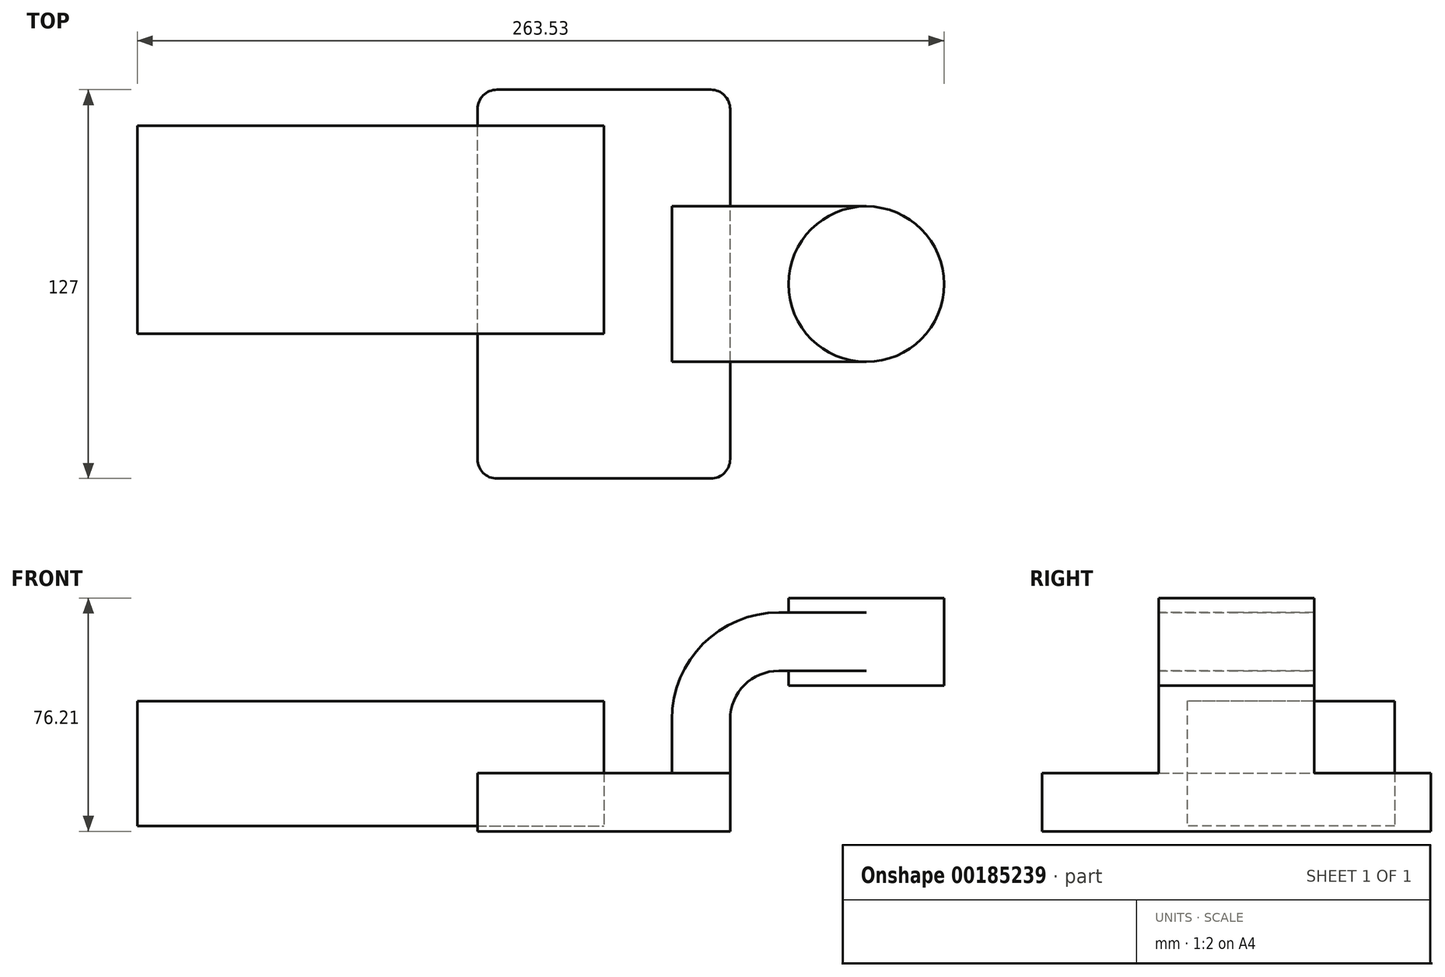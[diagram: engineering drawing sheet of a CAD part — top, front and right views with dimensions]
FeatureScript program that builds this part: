
annotation { "Feature Type Name" : "Feature", "Feature Type Description" : "" }
export const myFeature = defineFeature(function(context is Context, id is Id, definition is map)
    precondition{}
    {
        {
            var Q0;
            Q0=qCreatedBy(makeId("Front.planeOp"),FACE);
            var sketch = newSketch(context, id + "F0", { "sketchPlane" : qUnion([Q0])});
            skLineSegment(sketch, "E0.bottom", {"start": v(41.28, 9.53) * mm, "end": v(-41.28, 9.53) * mm});
            skLineSegment(sketch, "E0.top", {"start": v(41.28, -9.52) * mm, "end": v(-41.28, -9.52) * mm});
            skLineSegment(sketch, "E0.left", {"start": v(41.28, 9.53) * mm, "end": v(41.28, -9.52) * mm});
            skLineSegment(sketch, "E0.right", {"start": v(-41.28, 9.53) * mm, "end": v(-41.28, -9.52) * mm});
            skPoint(sketch, "E0.middle", {"position": v(0, 0) * mm});
            skLineSegment(sketch, "E1.bottom", {"start": v(111.12, 66.68) * mm, "end": v(60.32, 66.68) * mm});
            skLineSegment(sketch, "E1.top", {"start": v(111.12, 38.1) * mm, "end": v(60.33, 38.1) * mm});
            skLineSegment(sketch, "E1.left", {"start": v(111.12, 66.68) * mm, "end": v(111.12, 38.1) * mm});
            skLineSegment(sketch, "E1.right", {"start": v(60.32, 66.68) * mm, "end": v(60.33, 38.1) * mm});
            skPoint(sketch, "E1.middle", {"position": v(85.73, 52.39) * mm});
            skLineSegment(sketch, "E2", {"start": v(41.28, 9.53) * mm, "end": v(41.28, 27) * mm});
            skArc(sketch, "E3", {"start": v(41.28, 27) * mm, "mid": v(45.92, 38.23) * mm, "end": v(57.15, 42.88) * mm});
            skLineSegment(sketch, "E4", {"start": v(57.15, 42.88) * mm, "end": v(85.73, 42.88) * mm});
            skLineSegment(sketch, "E5.0", {"start": v(57.15, 61.93) * mm, "end": v(85.73, 61.93) * mm});
            skArc(sketch, "E5.1", {"start": v(22.23, 27) * mm, "mid": v(32.45, 51.7) * mm, "end": v(57.15, 61.93) * mm});
            skLineSegment(sketch, "E5.2", {"start": v(22.22, 9.53) * mm, "end": v(22.22, 27) * mm});
            skLineSegment(sketch, "E6", {"start": v(85.73, 38.1) * mm, "end": v(85.73, 66.68) * mm});
            skFitSpline(sketch, "E7", {"points": [v(-41.28, 9.53) * mm, v(57.15, 61.93) * mm], "startDerivative": vector(0, 58.53) * mm, "endDerivative": vector(117.35, 0) * mm});
            skSolve(sketch);
        }
        {
            var Q0;
            Q0=makeQuery(id+"F0.imprint","IMPRINT",FACE,{"disambiguationData":[TD([[makeQuery(id+"F0.imprint","IMPRINT",EDGE,{"derivedFrom":sQuery(id+"F0.wireOp",EDGE,"E0.top")}),-1.0]])]});
            extrude(context, id + "F1", {"entities" : qUnion([Q0]), "endBound" : BoundingType.SYMMETRIC, "depth" : 127 * mm});
        }
        {
            var Q0;
            {var subQ1=sQuery(id+"F0.wireOp",EDGE,"E2");Q0=makeQuery(id+"F0.imprint","IMPRINT",FACE,{"disambiguationData":[TD([[makeQuery(id+"F0.imprint","IMPRINT",EDGE,{"derivedFrom":subQ1}),1.0]])]});}
            var Q1;
            {var subQ0=sQuery(id+"F0.wireOp",EDGE,"E5.0");var subQ1=sQuery(id+"F0.wireOp",EDGE,"E1.right");var subQ2=makeQuery(id+"F0.imprint","INTERSECT",VERTEX,{"derivedFrom":[subQ1,subQ0]});Q1=makeQuery(id+"F0.imprint","IMPRINT",FACE,{"disambiguationData":[TD([[makeQuery(id+"F0.imprint","IMPRINT",EDGE,{"disambiguationData":[TD([[subQ2,-1.0]])],"derivedFrom":subQ1}),1.0]])]});}
            extrude(context, id + "F2", {"entities" : qUnion([Q0, Q1]), "operationType" : NewBodyOperationType.ADD, "endBound" : BoundingType.SYMMETRIC, "depth" : 50.8 * mm});
        }
        {
            var Q0;
            Q0=makeQuery(id+"F0.imprint","IMPRINT",FACE,{"disambiguationData":[TD([[makeQuery(id+"F0.imprint","IMPRINT",EDGE,{"derivedFrom":sQuery(id+"F0.wireOp",EDGE,"E5.1")}),1.0]])]});
            extrude(context, id + "F3", {"entities" : qUnion([Q0]), "operationType" : NewBodyOperationType.ADD, "endBound" : BoundingType.SYMMETRIC, "depth" : 15.88 * mm});
        }
        {
            var Q0;
            {var subQ0=sQuery(id+"F0.wireOp",EDGE,"E1.left");Q0=makeQuery(id+"F0.imprint","IMPRINT",FACE,{"disambiguationData":[TD([[makeQuery(id+"F0.imprint","IMPRINT",EDGE,{"derivedFrom":subQ0}),-1.0]])]});}
            var Q1;
            Q1=sQuery(id+"F0.wireOp",EDGE,"E6");
            revolve(context, id + "F4", {"operationType" : NewBodyOperationType.ADD, "entities" : qUnion([Q0]), "axis" : qUnion([Q1]), "revolveType" : RevolveType.FULL});
        }
        {
            var Q0;
            Q0=makeQuery(id+"F1.opExtrude","CAP_EDGE",EDGE,{"disambiguationData":[OSD([sQuery(id+"F0.wireOp",EDGE,"E0.left")])],"isStart":false});
            var Q1;
            Q1=makeQuery(id+"F1.opExtrude","CAP_EDGE",EDGE,{"disambiguationData":[OSD([sQuery(id+"F0.wireOp",EDGE,"E0.right")])],"isStart":false});
            var Q2;
            Q2=makeQuery(id+"F1.opExtrude","CAP_EDGE",EDGE,{"disambiguationData":[OSD([sQuery(id+"F0.wireOp",EDGE,"E0.left")])],"isStart":true});
            var Q3;
            Q3=makeQuery(id+"F1.opExtrude","CAP_EDGE",EDGE,{"disambiguationData":[OSD([sQuery(id+"F0.wireOp",EDGE,"E0.right")])],"isStart":true});
            fillet(context, id + "F5", {"entities" : qUnion([Q0, Q1, Q2, Q3]), "radius" : 6.35 * mm, "tangentPropagation" : true, "allowEdgeOverflow" : false});
        }
        {
            var Q0;
            Q0=qCreatedBy(makeId("Right.planeOp"),FACE);
            var sketch = newSketch(context, id + "F6", { "sketchPlane" : qUnion([Q0])});
            skLineSegment(sketch, "E8.bottom", {"start": v(51.69, 32.9) * mm, "end": v(-16.14, 32.9) * mm});
            skLineSegment(sketch, "E8.top", {"start": v(51.69, -7.76) * mm, "end": v(-16.14, -7.76) * mm});
            skLineSegment(sketch, "E8.left", {"start": v(51.69, 32.9) * mm, "end": v(51.69, -7.76) * mm});
            skLineSegment(sketch, "E8.right", {"start": v(-16.14, 32.9) * mm, "end": v(-16.14, -7.76) * mm});
            skSolve(sketch);
        }
        {
            var Q0;
            Q0=makeQuery(id+"F6.imprint","IMPRINT",FACE,{"disambiguationData":[TD([[makeQuery(id+"F6.imprint","IMPRINT",EDGE,{"derivedFrom":sQuery(id+"F6.wireOp",EDGE,"E8.bottom")}),1.0]])]});
            extrude(context, id + "F7", {"entities" : qUnion([Q0]), "oppositeDirection" : true, "depth" : 152.4 * mm});
        }
    });
